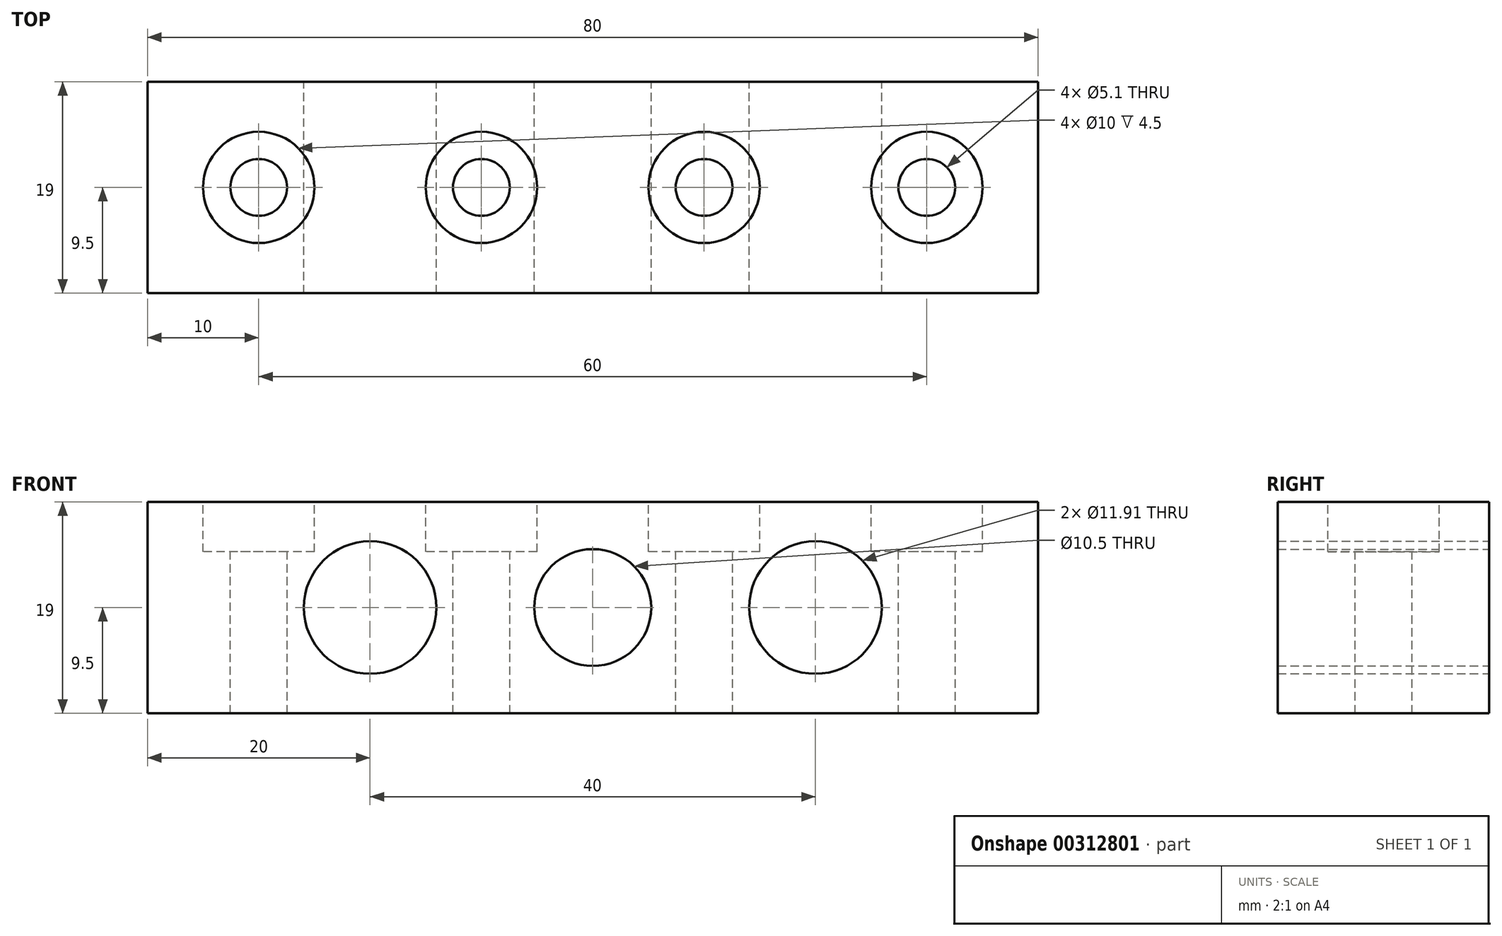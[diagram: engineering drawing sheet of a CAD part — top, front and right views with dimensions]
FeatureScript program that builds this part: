
annotation { "Feature Type Name" : "Feature", "Feature Type Description" : "" }
export const myFeature = defineFeature(function(context is Context, id is Id, definition is map)
    precondition{}
    {
        {
            var Q0;
            Q0=qCreatedBy(makeId("Top.planeOp"),FACE);
            var sketch = newSketch(context, id + "F0", { "sketchPlane" : qUnion([Q0])});
            skLineSegment(sketch, "E0.bottom", {"start": v(40, -9.5) * mm, "end": v(-40, -9.5) * mm});
            skLineSegment(sketch, "E0.top", {"start": v(40, 9.5) * mm, "end": v(-40, 9.5) * mm});
            skLineSegment(sketch, "E0.left", {"start": v(40, -9.5) * mm, "end": v(40, 9.5) * mm});
            skLineSegment(sketch, "E0.right", {"start": v(-40, -9.5) * mm, "end": v(-40, 9.5) * mm});
            skPoint(sketch, "E0.middle", {"position": v(0, 0) * mm});
            skSolve(sketch);
        }
        {
            var Q0;
            Q0=makeQuery(id+"F0.imprint","IMPRINT",FACE,{"disambiguationData":[TD([[makeQuery(id+"F0.imprint","IMPRINT",EDGE,{"derivedFrom":sQuery(id+"F0.wireOp",EDGE,"E0.bottom")}),-1.0]])]});
            extrude(context, id + "F1", {"entities" : qUnion([Q0]), "depth" : 19 * mm});
        }
        {
            var Q0;
            Q0=makeQuery(id+"F1.opExtrude","SWEPT_FACE",FACE,{"disambiguationData":[OSD([sQuery(id+"F0.wireOp",EDGE,"E0.top")])]});
            var sketch = newSketch(context, id + "F2", { "sketchPlane" : qUnion([Q0])});
            skLineSegment(sketch, "E1", {"start": v(-40, 9.5) * mm, "end": v(40, 9.5) * mm, "construction": true});
            skLineSegment(sketch, "E2", {"start": v(-30, 19) * mm, "end": v(-30, 0) * mm, "construction": true});
            skLineSegment(sketch, "E3", {"start": v(-10, 19) * mm, "end": v(-10, 0) * mm, "construction": true});
            skLineSegment(sketch, "E4", {"start": v(10, 19) * mm, "end": v(10, 0) * mm, "construction": true});
            skLineSegment(sketch, "E5", {"start": v(30, 19) * mm, "end": v(30, 0) * mm, "construction": true});
            skLineSegment(sketch, "E6", {"start": v(10, 19) * mm, "end": v(30, 0) * mm, "construction": true});
            skLineSegment(sketch, "E7", {"start": v(-10, 19) * mm, "end": v(-30, 0) * mm, "construction": true});
            skCircle(sketch, "E8", {"center": v(-20, 9.5) * mm, "radius": 5.96 * mm});
            skCircle(sketch, "E9", {"center": v(20, 9.5) * mm, "radius": 5.96 * mm});
            skCircle(sketch, "E10", {"center": v(0, 9.5) * mm, "radius": 5.25 * mm});
            skSolve(sketch);
        }
        {
            var Q0;
            Q0=makeQuery(id+"F2.imprint","IMPRINT",FACE,{"disambiguationData":[TD([[makeQuery(id+"F2.imprint","IMPRINT",EDGE,{"derivedFrom":sQuery(id+"F2.wireOp",EDGE,"E9")}),1.0]])]});
            var Q1;
            Q1=makeQuery(id+"F2.imprint","IMPRINT",FACE,{"disambiguationData":[TD([[makeQuery(id+"F2.imprint","IMPRINT",EDGE,{"derivedFrom":sQuery(id+"F2.wireOp",EDGE,"E8")}),1.0]])]});
            var Q2;
            Q2=makeQuery(id+"F2.imprint","IMPRINT",FACE,{"disambiguationData":[TD([[makeQuery(id+"F2.imprint","IMPRINT",EDGE,{"derivedFrom":sQuery(id+"F2.wireOp",EDGE,"E10")}),1.0]])]});
            extrude(context, id + "F3", {"entities" : qUnion([Q0, Q1, Q2]), "operationType" : NewBodyOperationType.REMOVE, "endBound" : BoundingType.THROUGH_ALL, "oppositeDirection" : true, "depth" : 12 * mm});
        }
        {
            var Q0;
            Q0=makeQuery(id+"F1.opExtrude","CAP_FACE",FACE,{"disambiguationData":[OSD([sQuery(id+"F0.wireOp",EDGE,"E0.bottom"),sQuery(id+"F0.wireOp",EDGE,"E0.top"),sQuery(id+"F0.wireOp",EDGE,"E0.left"),sQuery(id+"F0.wireOp",EDGE,"E0.right")])],"isStart":false});
            var sketch = newSketch(context, id + "F4", { "sketchPlane" : qUnion([Q0])});
            skLineSegment(sketch, "E11", {"start": v(-40, 0) * mm, "end": v(40, 0) * mm});
            skCircle(sketch, "E12", {"center": v(-30, 0) * mm, "radius": 2.55 * mm});
            skCircle(sketch, "E13.1.0.0", {"center": v(-10, 0) * mm, "radius": 2.55 * mm});
            skCircle(sketch, "E13.2.0.0", {"center": v(10, 0) * mm, "radius": 2.55 * mm});
            skCircle(sketch, "E13.3.0.0", {"center": v(30, 0) * mm, "radius": 2.55 * mm});
            skLineSegment(sketch, "E13.direction1", {"start": v(-30, 0) * mm, "end": v(-10, 0) * mm, "construction": true});
            skSolve(sketch);
        }
        {
            var Q0;
            Q0=qSketchRegion(id+"F4",true);
            extrude(context, id + "F5", {"entities" : qUnion([Q0]), "operationType" : NewBodyOperationType.REMOVE, "endBound" : BoundingType.THROUGH_ALL, "oppositeDirection" : true, "depth" : 25 * mm});
        }
        {
            var Q0;
            Q0=makeQuery(id+"F1.opExtrude","CAP_FACE",FACE,{"disambiguationData":[OSD([sQuery(id+"F0.wireOp",EDGE,"E0.bottom"),sQuery(id+"F0.wireOp",EDGE,"E0.top"),sQuery(id+"F0.wireOp",EDGE,"E0.left"),sQuery(id+"F0.wireOp",EDGE,"E0.right")])],"isStart":false});
            var sketch = newSketch(context, id + "F6", { "sketchPlane" : qUnion([Q0])});
            skCircle(sketch, "E14", {"center": v(-30, 0) * mm, "radius": 5 * mm});
            skCircle(sketch, "E15.1.0.0", {"center": v(-10, 0) * mm, "radius": 5 * mm});
            skCircle(sketch, "E15.2.0.0", {"center": v(10, 0) * mm, "radius": 5 * mm});
            skCircle(sketch, "E15.3.0.0", {"center": v(30, 0) * mm, "radius": 5 * mm});
            skLineSegment(sketch, "E15.direction1", {"start": v(-30, 0) * mm, "end": v(-10, 0) * mm, "construction": true});
            skSolve(sketch);
        }
        {
            var Q0;
            Q0=qSketchRegion(id+"F6",true);
            extrude(context, id + "F7", {"entities" : qUnion([Q0]), "operationType" : NewBodyOperationType.REMOVE, "oppositeDirection" : true, "depth" : 4.5 * mm});
        }
    });
